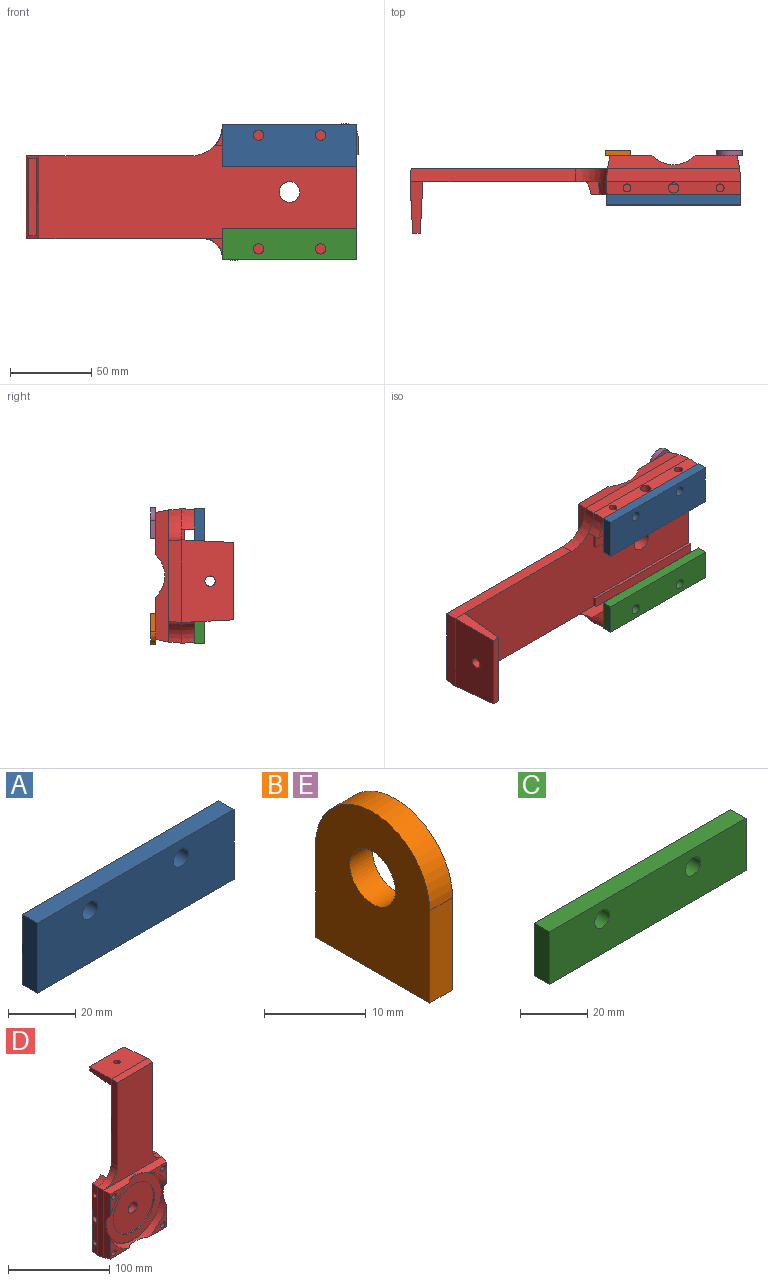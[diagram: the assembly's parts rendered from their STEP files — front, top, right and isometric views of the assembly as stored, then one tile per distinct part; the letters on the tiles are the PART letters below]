
ASSEMBLY  parts=5 mates=4
PART A: 8 faces, bbox 82.6x6.4x25.4 mm
  f0: plane 82.55x6.35mm, normal (0,0,1), area 524.2mm2, adj f1,f5,f6,f7
  f1: plane 25.4x6.35mm, normal (-1,0,0), area 161.3mm2, adj f0,f2,f6,f7
  f2: plane 82.55x6.35mm, normal (0,0,-1), area 524.2mm2, adj f1,f5,f6,f7
  f3: cylinder r=3.17mm len=6.35mm, axis (0,1,0), area 126.7mm2, adj f6,f7
  f4: cylinder r=3.17mm len=6.35mm, axis (0,1,0), area 126.7mm2, adj f6,f7
  f5: plane 25.4x6.35mm, normal (1,0,0), area 161.3mm2, adj f0,f2,f6,f7
  f6: plane 82.55x25.4mm, normal (0,-1,0), area 2033.4mm2, adj f0,f1,f2,f3,f4,f5
  f7: plane 82.55x25.4mm, normal (0,1,0), area 2033.4mm2, adj f0,f1,f2,f3,f4,f5
PART B: 7 faces, bbox 3.2x15.9x19.1 mm
  f0: plane 11.11x3.18mm, normal (0,1,0), area 35.3mm2, adj f1,f3,f5,f6
  f1: cylinder r=7.94mm len=15.88mm, axis (-1,0,0), area 79.2mm2, adj f0,f2,f5,f6
  f2: plane 11.11x3.18mm, normal (0,-1,0), area 35.3mm2, adj f1,f3,f5,f6
  f3: plane 15.88x3.18mm, normal (0,0,-1), area 50.4mm2, adj f0,f2,f5,f6
  f4: cylinder r=3.17mm len=6.35mm, axis (-1,0,0), area 63.3mm2, adj f5,f6
  f5: plane 19.05x15.88mm, normal (1,0,0), area 243.7mm2, adj f0,f1,f2,f3,f4
  f6: plane 19.05x15.88mm, normal (-1,0,0), area 243.7mm2, adj f0,f1,f2,f3,f4
PART C: 8 faces, bbox 82.6x6.4x19.1 mm
  f0: plane 19.05x6.35mm, normal (-1,0,0), area 121mm2, adj f1,f4,f6,f7
  f1: plane 82.55x6.35mm, normal (0,0,-1), area 524.2mm2, adj f0,f2,f6,f7
  f2: plane 19.05x6.35mm, normal (1,0,0), area 121mm2, adj f1,f4,f6,f7
  f3: cylinder r=3.17mm len=6.35mm, axis (0,1,0), area 126.7mm2, adj f6,f7
  f4: plane 82.55x6.35mm, normal (0,0,1), area 524.2mm2, adj f0,f2,f6,f7
  f5: cylinder r=3.17mm len=6.35mm, axis (0,1,0), area 126.7mm2, adj f6,f7
  f6: plane 82.55x19.05mm, normal (0,-1,0), area 1509.2mm2, adj f0,f1,f2,f3,f4,f5
  f7: plane 82.55x19.05mm, normal (0,1,0), area 1509.2mm2, adj f0,f1,f2,f3,f4,f5
PART D: 69 faces, bbox 82.6x47.7x203.3 mm
  f0: plane 25.6x12.62mm, normal (0,1,0), area 323mm2, adj f8,f32,f57,f59
  f1: plane 12.62x11.84mm, normal (0,1,0), area 149.4mm2, adj f8,f31,f32,f59
  f2: plane 12.62x11.84mm, normal (0,1,0), area 149.4mm2, adj f8,f25,f32,f58
  f3: plane 25.6x12.62mm, normal (0,1,0), area 323mm2, adj f8,f32,f57,f58
  f4: plane 79.38x79.38mm, normal (0,-1,0), area 387.9mm2, adj f38,f46
  f5: plane 120.64x81.16mm, normal (0,-1,0), area 6082.4mm2, adj f11,f12,f16,f17,f18,f43
  f6: plane 57.15x57.15mm, normal (0,-1,0), area 2438.5mm2, adj f36,f37
  f7: plane 195.26x57.15mm, normal (0,1,0), area 8802.8mm2, adj f8,f9,f11,f12,f14,f17,f20,f31
  f8: plane 87.32x7.94mm, normal (1,0,0), area 493.7mm2, adj f0,f1,f2,f3,f7,f24,f25,f27
  f9: plane 95.17x7.94mm, normal (-1,0,0), area 606.2mm2, adj f7,f10,f28,f30,f34,f35
  f10: plane 91.56x12.28mm, normal (0,1,0), area 972.9mm2, adj f9,f28,f29,f30,f53,f55
  f11: plane 101.6x7.94mm, normal (-1,-0.09,0), area 806.8mm2, adj f5,f7,f12,f18,f21
  f12: cone r=19.05mm half-angle=5deg, axis (0,-1,0), area 240mm2, adj f5,f7,f11,f13,f27
  f13: plane 82.56x7.95mm, normal (-1,-0.09,0), area 652.2mm2, adj f12,f14,f26,f44
  f14: plane 82.55x7.94mm, normal (0,-0.09,-1), area 652.2mm2, adj f7,f13,f15,f25,f28,f45
  f15: plane 82.57x7.96mm, normal (1,-0.09,0), area 652.3mm2, adj f14,f16,f29,f47
  f16: cone r=12.7mm half-angle=5deg, axis (0,-1,0), area 160.6mm2, adj f5,f15,f17,f30
  f17: plane 107.95x7.94mm, normal (1,-0.09,0), area 857.4mm2, adj f5,f7,f16,f18,f19
  f18: plane 50.8x7.94mm, normal (0,-0.09,1), area 399.2mm2, adj f5,f11,f17,f22
  f19: plane 31.75x7.94mm, normal (1,0.05,0), area 199.5mm2, adj f17,f20,f22,f23
  f20: plane 50.87x31.82mm, normal (0,0.05,-1), area 1530.5mm2, adj f7,f19,f21,f23,f60
  f21: plane 31.75x7.94mm, normal (-1,0.05,0), area 199.5mm2, adj f11,f20,f22,f23
  f22: plane 50.8x31.75mm, normal (0,0.05,1), area 1530.5mm2, adj f18,f19,f21,f23,f60
  f23: plane 47.47x4.61mm, normal (0,1,0), area 218.8mm2, adj f19,f20,f21,f22
  f24: plane 86.43x12.28mm, normal (0,1,0), area 959.4mm2, adj f8,f25,f26,f27,f49,f51
  f25: plane 25.4x7.94mm, normal (0,0.05,-1), area 119.4mm2, adj f2,f8,f14,f24,f26,f32
  f26: plane 82.57x7.96mm, normal (-1,0.05,0), area 584.5mm2, adj f13,f24,f25,f27,f57,f58,f59
  f27: cone r=19.05mm half-angle=3deg, axis (0,1,0), area 108.6mm2, adj f8,f12,f24,f26
  f28: plane 19.05x7.94mm, normal (0,0.05,-1), area 109.3mm2, adj f9,f10,f14,f29,f33,f35
  f29: plane 82.56x7.94mm, normal (1,0.05,0), area 652.9mm2, adj f10,f15,f28,f30
  f30: cone r=12.7mm half-angle=3deg, axis (0,1,0), area 142.1mm2, adj f9,f10,f16,f29
  f31: plane 12.7x1.59mm, normal (0,0.05,1), area 20.1mm2, adj f1,f7,f8,f32
  f32: plane 82.56x1.6mm, normal (1,0.05,0), area 128.1mm2, adj f0,f1,f2,f3,f7,f25,f31,f57
  f33: plane 82.55x1.59mm, normal (-1,0.05,0), area 131.1mm2, adj f7,f28,f34,f35
  f34: plane 6.35x1.59mm, normal (0,0.05,1), area 10mm2, adj f7,f9,f33,f35
  f35: plane 82.38x6.27mm, normal (0,1,0), area 516.3mm2, adj f9,f28,f33,f34
  f36: cylinder r=6.35mm len=12.7mm, axis (0,-1,0), area 316.7mm2, adj f6,f7
  f37: cone r=28.57mm half-angle=3deg, axis (0,-1,0), area 285.8mm2, adj f6,f39
  f38: cone r=38.1mm half-angle=3deg, axis (0,1,0), area 380.1mm2, adj f4,f39
  f39: plane 76.03x76.03mm, normal (0,-1,0), area 1960.3mm2, adj f37,f38
  f40: plane 25.8x25.78mm, normal (0,-1,0), area 196.4mm2, adj f44,f45,f46,f67
  f41: plane 25.79x25.78mm, normal (0,-1,0), area 196.2mm2, adj f43,f44,f46,f65
  f42: plane 25.79x25.78mm, normal (0,-1,0), area 196.3mm2, adj f43,f46,f47,f63
  f43: plane 81.16x7.95mm, normal (0,-0.19,0.98), area 542.6mm2, adj f5,f41,f42,f44,f46,f47
  f44: plane 81.17x7.95mm, normal (-0.98,-0.19,0), area 542.3mm2, adj f13,f40,f41,f43,f45,f46
  f45: plane 81.16x7.95mm, normal (0,-0.19,-0.98), area 542.8mm2, adj f14,f40,f44,f46,f47,f48
  f46: cone r=39.69mm half-angle=11deg, axis (0,-1,0), area 1645.6mm2, adj f4,f40,f41,f42,f43,f44,f45,f47
  f47: plane 81.18x7.95mm, normal (0.98,-0.19,0), area 542.3mm2, adj f15,f42,f43,f45,f46,f48
  f48: plane 25.8x25.78mm, normal (0,-1,0), area 196.4mm2, adj f45,f46,f47,f61
  f49: cylinder r=3.17mm len=9.53mm, axis (0,1,0), area 190mm2, adj f24,f50
  f50: plane 6.35x6.35mm, normal (0,1,0), area 31.7mm2, adj f49
  f51: cylinder r=3.17mm len=9.53mm, axis (0,1,0), area 190mm2, adj f24,f52
  f52: plane 6.35x6.35mm, normal (0,1,0), area 31.7mm2, adj f51
  f53: cylinder r=3.17mm len=9.53mm, axis (0,1,0), area 190mm2, adj f10,f54
  f54: plane 6.35x6.35mm, normal (0,1,0), area 31.7mm2, adj f53
  f55: cylinder r=3.17mm len=9.53mm, axis (0,1,0), area 190mm2, adj f10,f56
  f56: plane 6.35x6.35mm, normal (0,1,0), area 31.7mm2, adj f55
  f57: cylinder r=3.17mm len=25.33mm, axis (-1,0,0), area 310.9mm2, adj f0,f3,f8,f26,f32
  f58: cylinder r=2.41mm len=25.24mm, axis (-1,0,0), area 209.3mm2, adj f2,f3,f8,f26,f32
  f59: cylinder r=2.41mm len=25.24mm, axis (-1,0,0), area 209.3mm2, adj f0,f1,f8,f26,f32
  f60: cylinder r=3.17mm len=6.44mm, axis (0,0,-1), area 121.8mm2, adj f20,f22
  f61: cylinder r=3.17mm len=12.7mm, axis (0,-1,0), area 253.4mm2, adj f48,f62
  f62: plane 6.35x6.35mm, normal (0,-1,0), area 31.7mm2, adj f61
  f63: cylinder r=3.17mm len=12.7mm, axis (0,-1,0), area 253.4mm2, adj f42,f64
  f64: plane 6.35x6.35mm, normal (0,-1,0), area 31.7mm2, adj f63
  f65: cylinder r=3.17mm len=12.7mm, axis (0,-1,0), area 253.4mm2, adj f41,f66
  f66: plane 6.35x6.35mm, normal (0,-1,0), area 31.7mm2, adj f65
  f67: cylinder r=3.17mm len=12.7mm, axis (0,-1,0), area 253.4mm2, adj f40,f68
  f68: plane 6.35x6.35mm, normal (0,-1,0), area 31.7mm2, adj f67
PART E: same geometry as B
PLACE A t=(-41.27,-7.94,15.88)mm
PLACE B rot(axis=(0.71,-0.71,0),180deg) t=(-26.17,19.05,-22.98)mm
PLACE C rot(axis=(1,0,0),180deg) t=(-41.27,-14.29,-22.23)mm
PLACE D rot(axis=(0.71,0,-0.71),180deg) t=(41.28,0,41.28)mm
PLACE E rot(axis=(0,0,-1),90deg) t=(26.17,19.05,22.98)mm
MATE fastened E.f1 <-> D.f67  axis (0,-1,0) through (34.11,15.88,34.09)mm
MATE fastened B.f1 <-> D.f63  axis (0,-1,0) through (-34.1,15.88,-34.09)mm
MATE fastened A.f3 <-> D.f49  axis (0,1,0) through (-19.04,-7.94,34.92)mm
MATE fastened C.f3 <-> D.f55  axis (0,1,0) through (-19.04,-7.94,-34.93)mm
